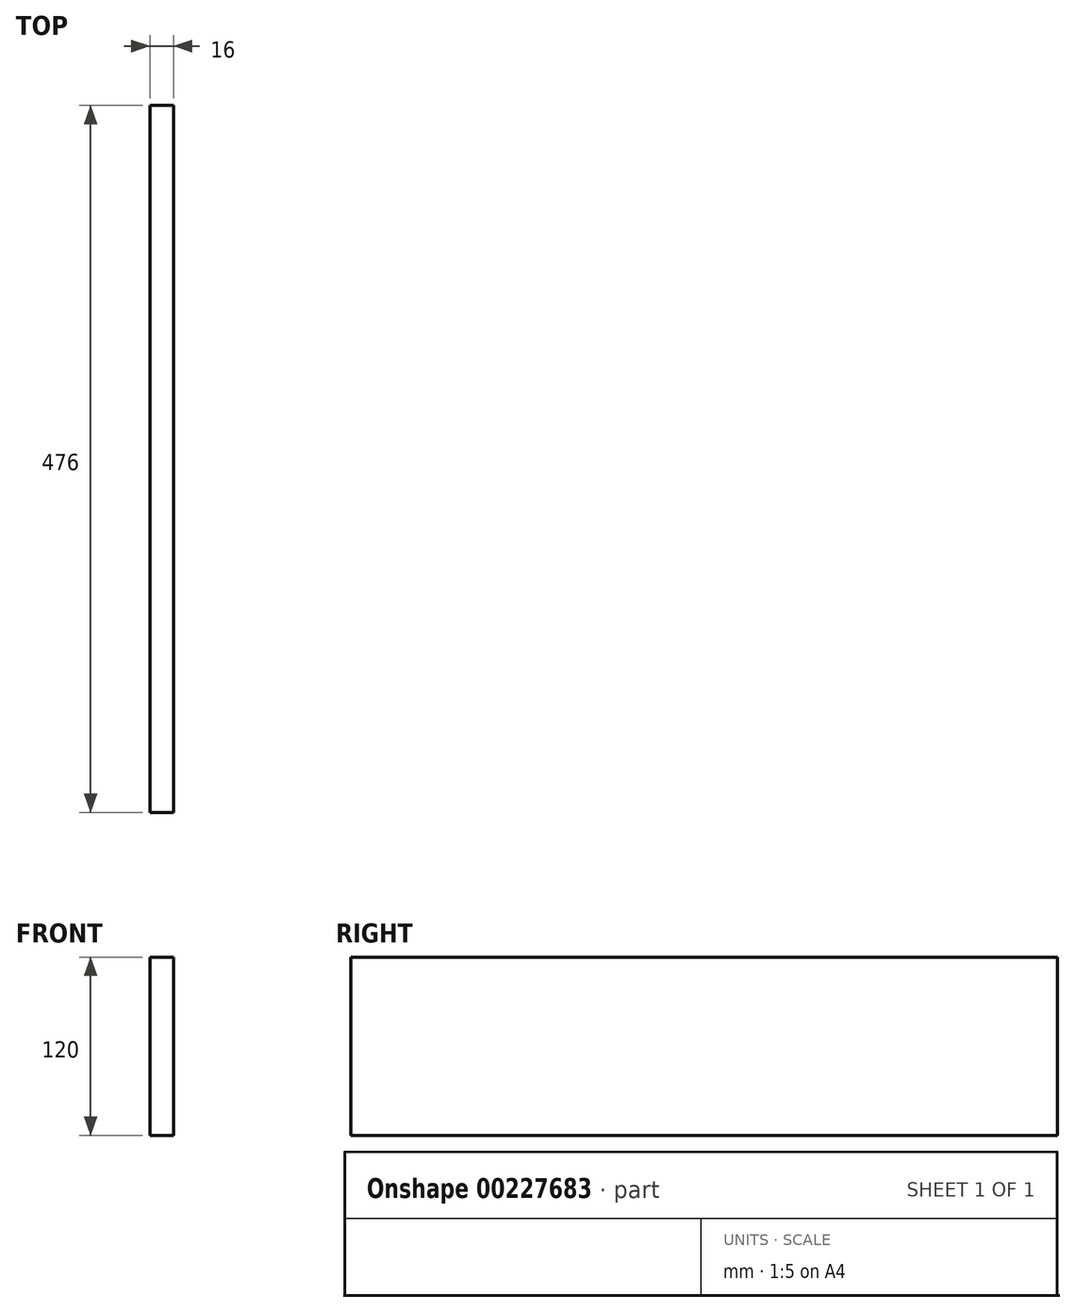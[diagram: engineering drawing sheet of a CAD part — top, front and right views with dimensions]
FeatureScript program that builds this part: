
annotation { "Feature Type Name" : "Feature", "Feature Type Description" : "" }
export const myFeature = defineFeature(function(context is Context, id is Id, definition is map)
    precondition{}
    {
        {
            var Q0;
            Q0=qCreatedBy(makeId("Right.planeOp"),FACE);
            var sketch = newSketch(context, id + "F0", { "sketchPlane" : qUnion([Q0])});
            skLineSegment(sketch, "E0.bottom", {"start": v(238, -60) * mm, "end": v(-238, -60) * mm});
            skLineSegment(sketch, "E0.top", {"start": v(238, 60) * mm, "end": v(-238, 60) * mm});
            skLineSegment(sketch, "E0.left", {"start": v(238, -60) * mm, "end": v(238, 60) * mm});
            skLineSegment(sketch, "E0.right", {"start": v(-238, -60) * mm, "end": v(-238, 60) * mm});
            skPoint(sketch, "E0.middle", {"position": v(0, 0) * mm});
            skSolve(sketch);
        }
        {
            var Q0;
            Q0 = qSketchRegion(id + "F0", true);
            extrude(context, id + "F1", {"entities" : qUnion([Q0]), "depth" : 16 * mm, "symmetric" : true});
        }
    });
